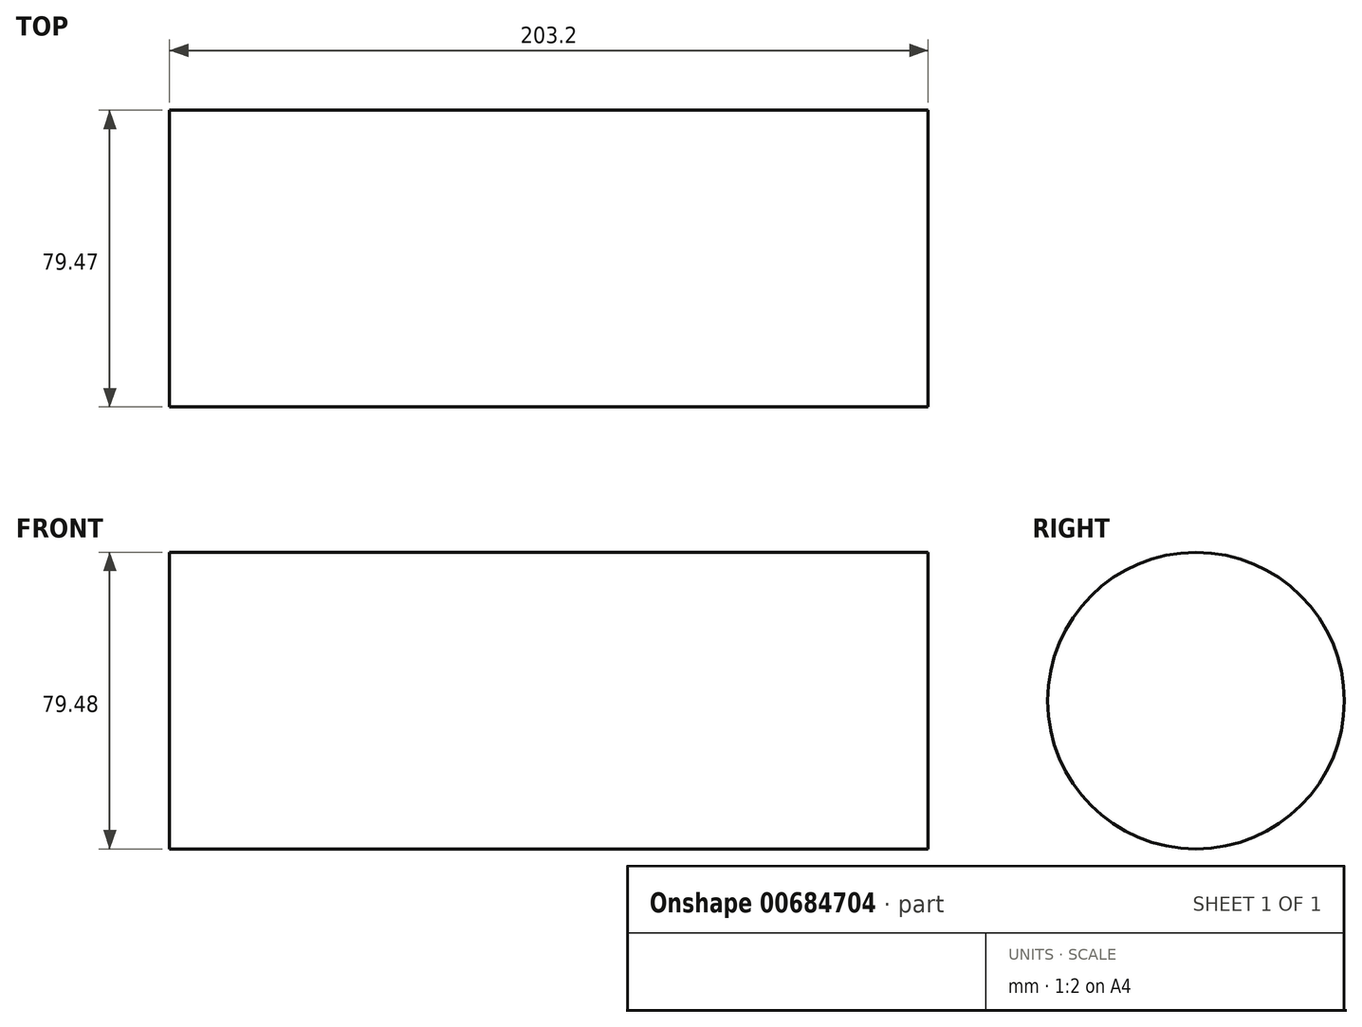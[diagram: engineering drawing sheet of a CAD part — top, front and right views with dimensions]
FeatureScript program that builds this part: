
annotation { "Feature Type Name" : "Feature", "Feature Type Description" : "" }
export const myFeature = defineFeature(function(context is Context, id is Id, definition is map)
    precondition{}
    {
        {
            var Q0;
            Q0=qCreatedBy(makeId("Right.planeOp"),FACE);
            var sketch = newSketch(context, id + "F0", { "sketchPlane" : qUnion([Q0])});
            skCircle(sketch, "E0", {"center": v(-15.57, 0) * mm, "radius": 39.74 * mm});
            skSolve(sketch);
        }
        {
            var Q0;
            Q0 = qSketchRegion(id + "F0", true);
            extrude(context, id + "F1", {"entities" : qUnion([Q0]), "depth" : 203.2 * mm, "offsetDistance" : 25.4 * mm});
        }
    });
